# Revit family: HARMANN - VENTIN VL STHY2
name_source: partatom
category: Akcesoria wentylacyjne
units: mm (PartAtom-declared; Revit-internal decimal feet)

## family parameters
Obiekt nadrzędny = Powierzchnia
Tnij formami wycięć po wczytaniu = Tak
Typ części = Łączy się z
Współdzielony = Nie
Wymiar okrągłego złącza = Użyj średnicy

## types (1)
- VENTIN VL STHY2
    Domyślna rzędna = 1219 mm
    Izolacyjność akustyczna nawiewnik otwarty D n,e,w (C, Ctr) = 57 (-2;-5) dB
    Izolacyjność akustyczna nawiewnik przymkniety D n,e,w (C, Ctr) = 58 (-2;-5) dB
    Kierunek przepływu = Przepływ powietrza z zewnętrz do pomieszczenia (przepływ in-line)
    Max Flow = 36.3 m³/h
    Min Flow = 7.2 m³/h
    Model = VENTIN VL STHY2
    Montaż = Nawiewniki VENTIN VL STHY2 przeznaczone są do montażu z przepływem in-line w ścianach zewnętrznych budynków mieszkalnych, zamieszkania zbiorowego i użyteczności publicznej.
    Numer artykułu = 04251400
    Opis = Nawiewnik ścienne przelotowy higrosterowany, akustyczny, z dodatkowym wytłumieniem,  VENTIN VL STHY2
    Producent = Harmann Polska Sp. z o.o.
    URL = https://harmann.pl
    Wydajność nawiewnika otwartego (dP=10Pa) = 27.0 m³/h
    Wydajność nawiewnika otwartego (dP=20Pa) = 36.3 m³/h
    Wydajność nawiewnika przymkniętego (dP=10Pa) = 7.2 m³/h
    Wydajność nawiewnika przymkniętego (dP=20Pa) = 10.4 m³/h
    Zastosowanie = Głównym zastosowaniem jest doprowadzenie powietrza kompensacyjnego do mieszkań, w systemowych rozwiązaniach mechanicznej wentylacji wywiewnej- SENSOVENT. Może być również wykorzystany w pomieszczeniach z wentylacją grawitacyjną, lub hybrydową. Nawiewniki ścienne można stosować w pomieszczeniach przeznaczonych na stały lub czasowy pobyt ludzi w budynkach mieszkalnych, zamieszkania zbiorowego, użyteczności publicznej, biurowych a także produkcyjnych i magazynowych.

## geometry (parser evidence)
native form markers: Sweep x2
no freeform markers — native parametric forms only
